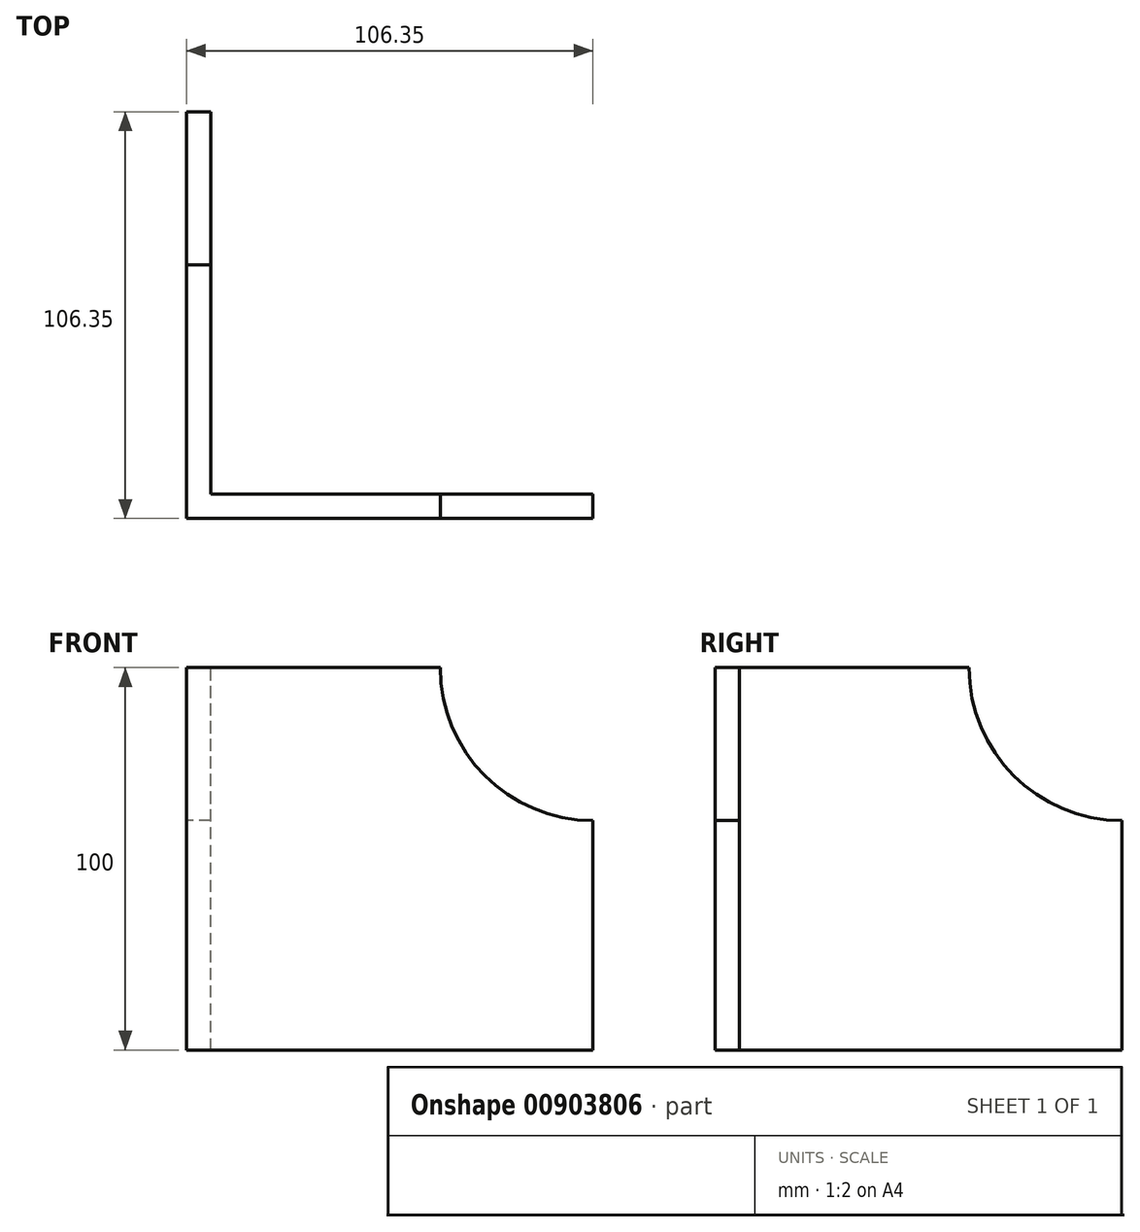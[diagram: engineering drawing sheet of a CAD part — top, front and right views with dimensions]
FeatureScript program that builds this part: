
annotation { "Feature Type Name" : "Feature", "Feature Type Description" : "" }
export const myFeature = defineFeature(function(context is Context, id is Id, definition is map)
    precondition{}
    {
        {
            var Q0;
            Q0=qCreatedBy(makeId("Front.planeOp"),FACE);
            var sketch = newSketch(context, id + "F0", { "sketchPlane" : qUnion([Q0])});
            skLineSegment(sketch, "E0.bottom", {"start": v(50, -50) * mm, "end": v(-50, -50) * mm});
            skLineSegment(sketch, "E0.top", {"start": v(50, 50) * mm, "end": v(-50, 50) * mm});
            skLineSegment(sketch, "E0.left", {"start": v(50, -50) * mm, "end": v(50, 50) * mm});
            skLineSegment(sketch, "E0.right", {"start": v(-50, -50) * mm, "end": v(-50, 50) * mm});
            skPoint(sketch, "E0.middle", {"position": v(0, 0) * mm});
            skSolve(sketch);
        }
        {
            var Q0;
            Q0=qSketchRegion(id+"F0",true);
            extrude(context, id + "F1", {"entities" : qUnion([Q0]), "depth" : 6.35 * mm, "offsetDistance" : 25 * mm});
        }
        {
            var Q0;
            Q0=makeQuery(id+"F1.opExtrude","SWEPT_FACE",FACE,{"disambiguationData":[OSD([sQuery(id+"F0.wireOp",EDGE,"E0.right")])]});
            var sketch = newSketch(context, id + "F2", { "sketchPlane" : qUnion([Q0])});
            skLineSegment(sketch, "E1.bottom", {"start": v(6.35, -50) * mm, "end": v(-100, -50) * mm});
            skLineSegment(sketch, "E1.top", {"start": v(6.35, 50) * mm, "end": v(-100, 50) * mm});
            skLineSegment(sketch, "E1.left", {"start": v(6.35, -50) * mm, "end": v(6.35, 50) * mm});
            skLineSegment(sketch, "E1.right", {"start": v(-100, -50) * mm, "end": v(-100, 50) * mm});
            skPoint(sketch, "E2", {"position": v(0, -50) * mm});
            skSolve(sketch);
        }
        {
            var Q0;
            Q0=qSketchRegion(id+"F2",true);
            extrude(context, id + "F3", {"entities" : qUnion([Q0]), "operationType" : NewBodyOperationType.ADD, "depth" : 6.35 * mm, "offsetDistance" : 25 * mm});
        }
        {
            var Q0;
            Q0=makeQuery(id+"F3.boolean.opBoolean","MERGE",FACE,{"derivedFrom":[makeQuery(id+"F1.opExtrude","CAP_FACE",FACE,{"disambiguationData":[OSD([sQuery(id+"F0.wireOp",EDGE,"E0.bottom"),sQuery(id+"F0.wireOp",EDGE,"E0.top"),sQuery(id+"F0.wireOp",EDGE,"E0.left"),sQuery(id+"F0.wireOp",EDGE,"E0.right")])],"isStart":false}),makeQuery(id+"F3.opExtrude","SWEPT_FACE",FACE,{"disambiguationData":[OSD([sQuery(id+"F2.wireOp",EDGE,"E1.left")])]})]});
            var sketch = newSketch(context, id + "F4", { "sketchPlane" : qUnion([Q0])});
            skArc(sketch, "E3", {"start": v(10, 50) * mm, "mid": v(21.72, 21.72) * mm, "end": v(50, 10) * mm});
            skLineSegment(sketch, "E4", {"start": v(10, 50) * mm, "end": v(50, 50) * mm});
            skLineSegment(sketch, "E5", {"start": v(50, 10) * mm, "end": v(50, 50) * mm});
            skSolve(sketch);
        }
        {
            var Q0;
            Q0=makeQuery(id+"F3.opExtrude","CAP_FACE",FACE,{"disambiguationData":[OSD([sQuery(id+"F2.wireOp",EDGE,"E1.bottom"),sQuery(id+"F2.wireOp",EDGE,"E1.top"),sQuery(id+"F2.wireOp",EDGE,"E1.left"),sQuery(id+"F2.wireOp",EDGE,"E1.right")])],"isStart":false});
            var sketch = newSketch(context, id + "F5", { "sketchPlane" : qUnion([Q0])});
            skArc(sketch, "E6", {"start": v(-100, 10) * mm, "mid": v(-71.72, 21.72) * mm, "end": v(-60, 50) * mm});
            skLineSegment(sketch, "E7", {"start": v(-100, 10) * mm, "end": v(-100, 50) * mm});
            skLineSegment(sketch, "E8", {"start": v(-60, 50) * mm, "end": v(-100, 50) * mm});
            skSolve(sketch);
        }
        {
            var Q0;
            Q0=qSketchRegion(id+"F5",true);
            extrude(context, id + "F6", {"entities" : qUnion([Q0]), "operationType" : NewBodyOperationType.REMOVE, "oppositeDirection" : true, "depth" : 25 * mm, "offsetDistance" : 25 * mm});
        }
        {
            var Q0;
            Q0=makeQuery(id+"F4.imprint","IMPRINT",FACE,{"disambiguationData":[TD([[makeQuery(id+"F4.imprint","IMPRINT",EDGE,{"derivedFrom":sQuery(id+"F4.wireOp",EDGE,"E3")}),1.0]])]});
            extrude(context, id + "F7", {"entities" : qUnion([Q0]), "operationType" : NewBodyOperationType.REMOVE, "oppositeDirection" : true, "depth" : 25 * mm, "offsetDistance" : 25 * mm});
        }
    });
